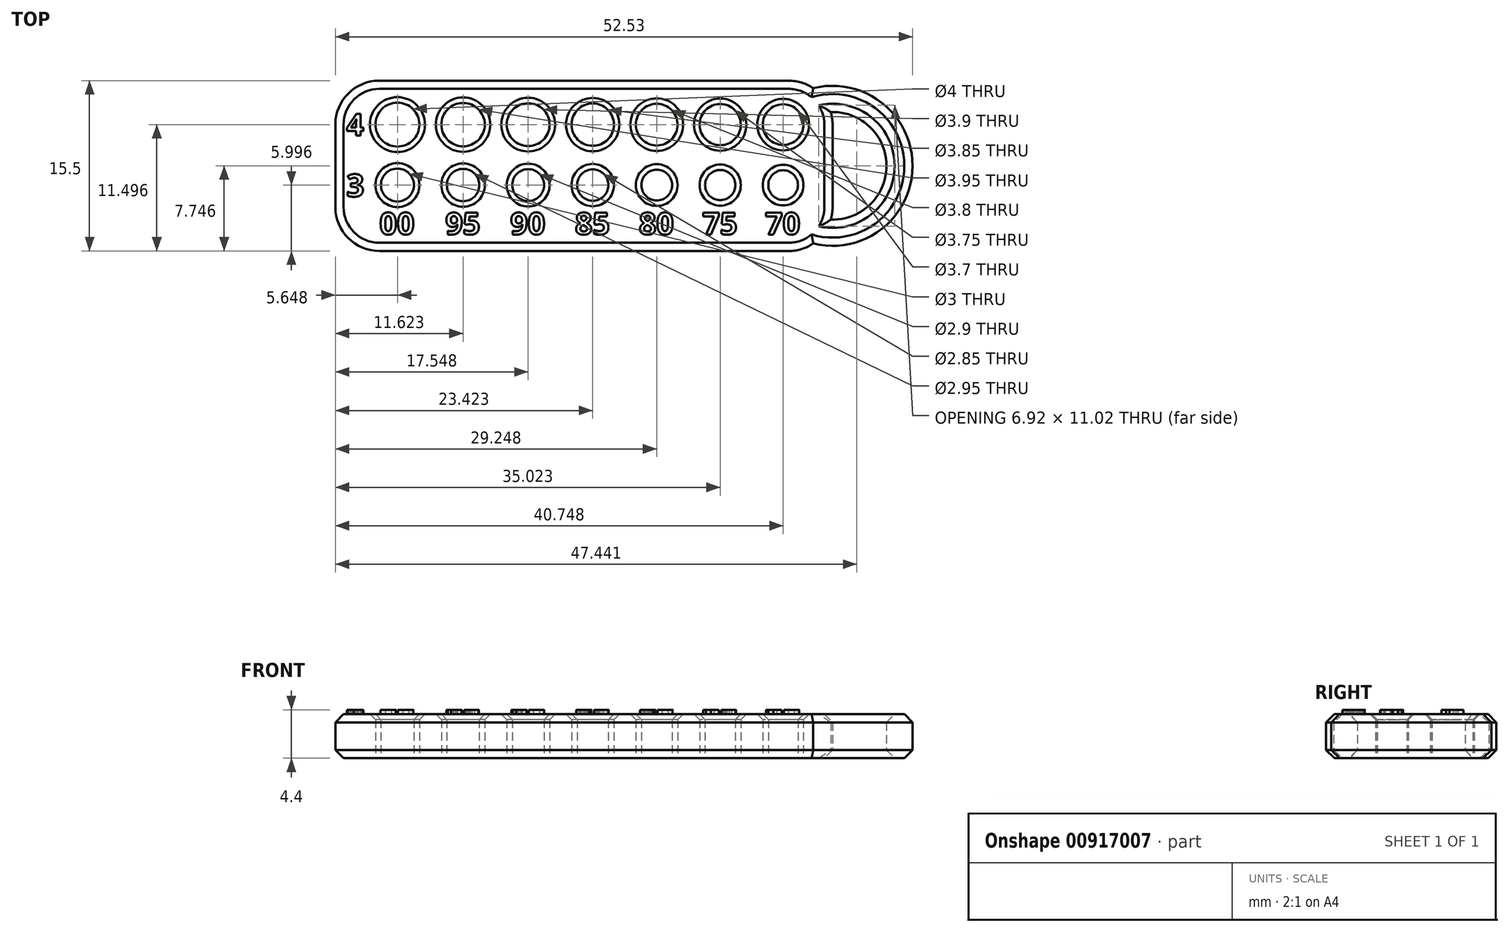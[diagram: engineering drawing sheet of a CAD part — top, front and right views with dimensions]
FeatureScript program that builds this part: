
annotation { "Feature Type Name" : "Feature", "Feature Type Description" : "" }
export const myFeature = defineFeature(function(context is Context, id is Id, definition is map)
    precondition{}
    {
        {
            var Q0;
            Q0=qCreatedBy(makeId("Top.planeOp"),FACE);
            var sketch = newSketch(context, id + "F0", { "sketchPlane" : qUnion([Q0])});
            skCircle(sketch, "E0", {"center": v(-62.61, 29.83) * mm, "radius": 2 * mm});
            skLineSegment(sketch, "E1", {"start": v(-65.55, 29.83) * mm, "end": v(-24.42, 29.83) * mm, "construction": true});
            skCircle(sketch, "E2", {"center": v(-50.71, 29.83) * mm, "radius": 1.95 * mm});
            skCircle(sketch, "E3", {"center": v(-44.84, 29.83) * mm, "radius": 1.93 * mm});
            skCircle(sketch, "E4", {"center": v(-56.64, 29.83) * mm, "radius": 1.98 * mm});
            skCircle(sketch, "E5", {"center": v(-39.01, 29.83) * mm, "radius": 1.9 * mm});
            skCircle(sketch, "E6", {"center": v(-33.24, 29.83) * mm, "radius": 1.88 * mm});
            skCircle(sketch, "E7", {"center": v(-27.51, 29.83) * mm, "radius": 1.85 * mm});
            skCircle(sketch, "E8", {"center": v(-62.61, 24.33) * mm, "radius": 1.5 * mm});
            skLineSegment(sketch, "E9", {"start": v(-65.55, 24.33) * mm, "end": v(-24.99, 24.33) * mm, "construction": true});
            skCircle(sketch, "E10", {"center": v(-50.71, 24.33) * mm, "radius": 1.45 * mm});
            skCircle(sketch, "E11", {"center": v(-44.84, 24.33) * mm, "radius": 1.43 * mm});
            skCircle(sketch, "E12", {"center": v(-56.64, 24.33) * mm, "radius": 1.48 * mm});
            skCircle(sketch, "E13", {"center": v(-39.01, 24.33) * mm, "radius": 1.4 * mm});
            skCircle(sketch, "E14", {"center": v(-33.24, 24.33) * mm, "radius": 1.38 * mm});
            skCircle(sketch, "E15", {"center": v(-27.51, 24.33) * mm, "radius": 1.35 * mm});
            skLineSegment(sketch, "E16.bottom", {"start": v(-64.26, 33.83) * mm, "end": v(-27.01, 33.83) * mm});
            skLineSegment(sketch, "E16.top", {"start": v(-64.26, 18.33) * mm, "end": v(-27.01, 18.33) * mm});
            skLineSegment(sketch, "E16.left", {"start": v(-68.26, 29.83) * mm, "end": v(-68.26, 22.33) * mm});
            skLineSegment(sketch, "E16.right", {"start": v(-23.01, 29.83) * mm, "end": v(-23.01, 22.33) * mm});
            skPoint(sketch, "E17.visualSharp", {"position": v(-68.26, 33.83) * mm});
            skArc(sketch, "E17.filletArc", {"start": v(-64.26, 33.83) * mm, "mid": v(-67.09, 32.65) * mm, "end": v(-68.26, 29.83) * mm});
            skPoint(sketch, "E18.visualSharp", {"position": v(-68.26, 18.33) * mm});
            skArc(sketch, "E18.filletArc", {"start": v(-68.26, 22.33) * mm, "mid": v(-67.09, 19.5) * mm, "end": v(-64.26, 18.33) * mm});
            skPoint(sketch, "E19.visualSharp", {"position": v(-23.01, 18.33) * mm});
            skArc(sketch, "E19.filletArc", {"start": v(-27.01, 18.33) * mm, "mid": v(-25.84, 18.5) * mm, "end": v(-24.77, 19.01) * mm});
            skPoint(sketch, "E20.visualSharp", {"position": v(-23.01, 33.83) * mm});
            skArc(sketch, "E20.filletArc", {"start": v(-23.01, 29.83) * mm, "mid": v(-23.05, 30.4) * mm, "end": v(-23.18, 30.98) * mm});
            skPoint(sketch, "E21", {"position": v(-60.61, 29.83) * mm});
            skPoint(sketch, "E22", {"position": v(-58.61, 29.83) * mm});
            skPoint(sketch, "E23", {"position": v(-54.66, 29.83) * mm});
            skPoint(sketch, "E24", {"position": v(-52.66, 29.83) * mm});
            skPoint(sketch, "E25", {"position": v(-48.76, 29.83) * mm});
            skPoint(sketch, "E26", {"position": v(-46.76, 29.83) * mm});
            skPoint(sketch, "E27", {"position": v(-42.91, 29.83) * mm});
            skPoint(sketch, "E28", {"position": v(-40.91, 29.83) * mm});
            skPoint(sketch, "E29", {"position": v(-37.11, 29.83) * mm});
            skPoint(sketch, "E30", {"position": v(-35.11, 29.83) * mm});
            skPoint(sketch, "E31", {"position": v(-31.36, 29.83) * mm});
            skPoint(sketch, "E32", {"position": v(-29.36, 29.83) * mm});
            skArc(sketch, "E33", {"start": v(-24.77, 19.01) * mm, "mid": v(-15.73, 26.08) * mm, "end": v(-24.77, 33.14) * mm});
            skArc(sketch, "E34", {"start": v(-25.7, 30.18) * mm, "mid": v(-25.94, 30) * mm, "end": v(-26.17, 29.83) * mm});
            skArc(sketch, "E35.trimOffspring", {"start": v(-23.18, 21.18) * mm, "mid": v(-18.1, 26.08) * mm, "end": v(-23.18, 30.98) * mm});
            skArc(sketch, "E36.trimOffspring", {"start": v(-23.18, 21.18) * mm, "mid": v(-23.05, 21.75) * mm, "end": v(-23.01, 22.33) * mm});
            skArc(sketch, "E37.trimOffspring", {"start": v(-29.25, 29.83) * mm, "mid": v(-29.3, 29.74) * mm, "end": v(-29.35, 29.65) * mm});
            skArc(sketch, "E38.trimOffspring", {"start": v(-24.77, 33.14) * mm, "mid": v(-25.84, 33.65) * mm, "end": v(-27.01, 33.83) * mm});
            skSolve(sketch);
        }
        {
            var Q0;
            Q0=makeQuery(id+"F0.imprint","IMPRINT",FACE,{"disambiguationData":[TD([[makeQuery(id+"F0.imprint","IMPRINT",EDGE,{"derivedFrom":sQuery(id+"F0.wireOp",EDGE,"E0")}),-1.0]])]});
            extrude(context, id + "F1", {"entities" : qUnion([Q0]), "depth" : 4 * mm, "offsetDistance" : 25 * mm});
        }
        {
            var Q0;
            Q0=makeQuery(id+"F1.opExtrude","CAP_FACE",FACE,{"disambiguationData":[OSD([sQuery(id+"F0.wireOp",EDGE,"E0"),sQuery(id+"F0.wireOp",EDGE,"E2"),sQuery(id+"F0.wireOp",EDGE,"E3"),sQuery(id+"F0.wireOp",EDGE,"E4"),sQuery(id+"F0.wireOp",EDGE,"E5"),sQuery(id+"F0.wireOp",EDGE,"E6"),sQuery(id+"F0.wireOp",EDGE,"E7"),sQuery(id+"F0.wireOp",EDGE,"E8"),sQuery(id+"F0.wireOp",EDGE,"E10"),sQuery(id+"F0.wireOp",EDGE,"E11"),sQuery(id+"F0.wireOp",EDGE,"E12"),sQuery(id+"F0.wireOp",EDGE,"E13"),sQuery(id+"F0.wireOp",EDGE,"E14"),sQuery(id+"F0.wireOp",EDGE,"E15"),sQuery(id+"F0.wireOp",EDGE,"E16.bottom"),sQuery(id+"F0.wireOp",EDGE,"E16.top"),sQuery(id+"F0.wireOp",EDGE,"E16.left"),sQuery(id+"F0.wireOp",EDGE,"E16.right"),sQuery(id+"F0.wireOp",EDGE,"E17.filletArc"),sQuery(id+"F0.wireOp",EDGE,"E18.filletArc"),sQuery(id+"F0.wireOp",EDGE,"E19.filletArc"),sQuery(id+"F0.wireOp",EDGE,"E20.filletArc")])],"isStart":false});
            var sketch = newSketch(context, id + "F2", { "sketchPlane" : qUnion([Q0])});
            skText(sketch, "E39", { "text": "3", "fontName": "OpenSans-Bold.ttf"});
            skText(sketch, "E40", { "text": "4", "fontName": "OpenSans-Bold.ttf"});
            skText(sketch, "E41", { "text": "00", "fontName": "OpenSans-Bold.ttf"});
            skText(sketch, "E42", { "text": "95", "fontName": "OpenSans-Bold.ttf"});
            skLineSegment(sketch, "E43", {"start": v(-70.1, 21.83) * mm, "end": v(-20.77, 21.83) * mm, "construction": true});
            skText(sketch, "E44", { "text": "90", "fontName": "OpenSans-Bold.ttf"});
            skLineSegment(sketch, "E45", {"start": v(-70.1, 19.83) * mm, "end": v(-20.77, 19.83) * mm, "construction": true});
            skText(sketch, "E46", { "text": "85", "fontName": "OpenSans-Bold.ttf"});
            skText(sketch, "E47", { "text": "80", "fontName": "OpenSans-Bold.ttf"});
            skText(sketch, "E48", { "text": "75", "fontName": "OpenSans-Bold.ttf"});
            skText(sketch, "E49", { "text": "70", "fontName": "OpenSans-Bold.ttf"});
            const initialGuessF2  = {"E39": [-0.06726, 0.02328, 1, 0, 0.00204], "E40": [-0.06726, 0.02883, 1, 0, 0.002], "E41": [-0.06424, 0.01983, 1, 0, 0.002], "E42": [-0.05825, 0.01983, 1, 0, 0.002], "E44": [-0.05234, 0.01983, 1, 0, 0.002], "E46": [-0.04645, 0.01983, 1, 0, 0.002], "E47": [-0.04064, 0.01983, 1, 0, 0.002], "E48": [-0.03485, 0.01983, 1, 0, 0.002], "E49": [-0.02914, 0.01983, 1, 0, 0.002]};
            skSetInitialGuess(sketch, initialGuessF2);
            skSolve(sketch);
        }
        {
            var Q0;
            Q0 = qSketchRegion(id + "F2", true);
            extrude(context, id + "F3", {"entities" : qUnion([Q0]), "operationType" : NewBodyOperationType.ADD, "depth" : 0.4 * mm, "offsetDistance" : 25 * mm});
        }
        {
            var Q0;
            Q0=makeQuery(id+"F1.opExtrude","CAP_EDGE",EDGE,{"disambiguationData":[OSD([sQuery(id+"F0.wireOp",EDGE,"E0")])],"isStart":false});
            var Q1;
            Q1=makeQuery(id+"F1.opExtrude","CAP_EDGE",EDGE,{"disambiguationData":[OSD([sQuery(id+"F0.wireOp",EDGE,"E4")])],"isStart":false});
            var Q2;
            Q2=makeQuery(id+"F1.opExtrude","CAP_EDGE",EDGE,{"disambiguationData":[OSD([sQuery(id+"F0.wireOp",EDGE,"E2")])],"isStart":false});
            var Q3;
            Q3=makeQuery(id+"F1.opExtrude","CAP_EDGE",EDGE,{"disambiguationData":[OSD([sQuery(id+"F0.wireOp",EDGE,"E3")])],"isStart":false});
            var Q4;
            Q4=makeQuery(id+"F1.opExtrude","CAP_EDGE",EDGE,{"disambiguationData":[OSD([sQuery(id+"F0.wireOp",EDGE,"E5")])],"isStart":false});
            var Q5;
            Q5=makeQuery(id+"F1.opExtrude","CAP_EDGE",EDGE,{"disambiguationData":[OSD([sQuery(id+"F0.wireOp",EDGE,"E6")])],"isStart":false});
            var Q6;
            Q6=makeQuery(id+"F1.opExtrude","CAP_EDGE",EDGE,{"disambiguationData":[OSD([sQuery(id+"F0.wireOp",EDGE,"E7")])],"isStart":false});
            var Q7;
            Q7=makeQuery(id+"F1.opExtrude","CAP_EDGE",EDGE,{"disambiguationData":[OSD([sQuery(id+"F0.wireOp",EDGE,"E15")])],"isStart":false});
            var Q8;
            Q8=makeQuery(id+"F1.opExtrude","CAP_EDGE",EDGE,{"disambiguationData":[OSD([sQuery(id+"F0.wireOp",EDGE,"E14")])],"isStart":false});
            var Q9;
            Q9=makeQuery(id+"F1.opExtrude","CAP_EDGE",EDGE,{"disambiguationData":[OSD([sQuery(id+"F0.wireOp",EDGE,"E13")])],"isStart":false});
            var Q10;
            Q10=makeQuery(id+"F1.opExtrude","CAP_EDGE",EDGE,{"disambiguationData":[OSD([sQuery(id+"F0.wireOp",EDGE,"E11")])],"isStart":false});
            var Q11;
            Q11=makeQuery(id+"F1.opExtrude","CAP_EDGE",EDGE,{"disambiguationData":[OSD([sQuery(id+"F0.wireOp",EDGE,"E10")])],"isStart":false});
            var Q12;
            Q12=makeQuery(id+"F1.opExtrude","CAP_EDGE",EDGE,{"disambiguationData":[OSD([sQuery(id+"F0.wireOp",EDGE,"E12")])],"isStart":false});
            var Q13;
            Q13=makeQuery(id+"F1.opExtrude","CAP_EDGE",EDGE,{"disambiguationData":[OSD([sQuery(id+"F0.wireOp",EDGE,"E8")])],"isStart":false});
            chamfer(context, id + "F4", {"entities" : qUnion([Q0, Q1, Q2, Q3, Q4, Q5, Q6, Q7, Q8, Q9, Q10, Q11, Q12, Q13]), "width" : 0.5 * mm, "tangentPropagation" : true});
        }
        {
            var Q0;
            Q0=makeQuery(id+"F1.opExtrude","CAP_EDGE",EDGE,{"disambiguationData":[OSD([sQuery(id+"F0.wireOp",EDGE,"E16.bottom")])],"isStart":false});
            var Q1;
            Q1=makeQuery(id+"F1.opExtrude","CAP_EDGE",EDGE,{"disambiguationData":[OSD([sQuery(id+"F0.wireOp",EDGE,"E33")])],"isStart":false});
            var Q2;
            Q2=makeQuery(id+"F1.opExtrude","CAP_EDGE",EDGE,{"disambiguationData":[OSD([sQuery(id+"F0.wireOp",EDGE,"E33")])],"isStart":true});
            var Q3;
            Q3=makeQuery(id+"F1.opExtrude","CAP_EDGE",EDGE,{"disambiguationData":[OSD([sQuery(id+"F0.wireOp",EDGE,"E16.top")])],"isStart":true});
            var Q4;
            Q4=makeQuery(id+"F1.opExtrude","CAP_EDGE",EDGE,{"disambiguationData":[OSD([sQuery(id+"F0.wireOp",EDGE,"E16.right")])],"isStart":false});
            var Q5;
            Q5=makeQuery(id+"F1.opExtrude","CAP_EDGE",EDGE,{"disambiguationData":[OSD([sQuery(id+"F0.wireOp",EDGE,"E35.trimOffspring")])],"isStart":false});
            var Q6;
            Q6=makeQuery(id+"F1.opExtrude","CAP_EDGE",EDGE,{"disambiguationData":[OSD([sQuery(id+"F0.wireOp",EDGE,"E16.right")])],"isStart":true});
            var Q7;
            Q7=makeQuery(id+"F1.opExtrude","CAP_EDGE",EDGE,{"disambiguationData":[OSD([sQuery(id+"F0.wireOp",EDGE,"E35.trimOffspring")])],"isStart":true});
            chamfer(context, id + "F5", {"entities" : qUnion([Q0, Q1, Q2, Q3, Q4, Q5, Q6, Q7]), "width" : 0.75 * mm, "tangentPropagation" : true});
        }
    });
